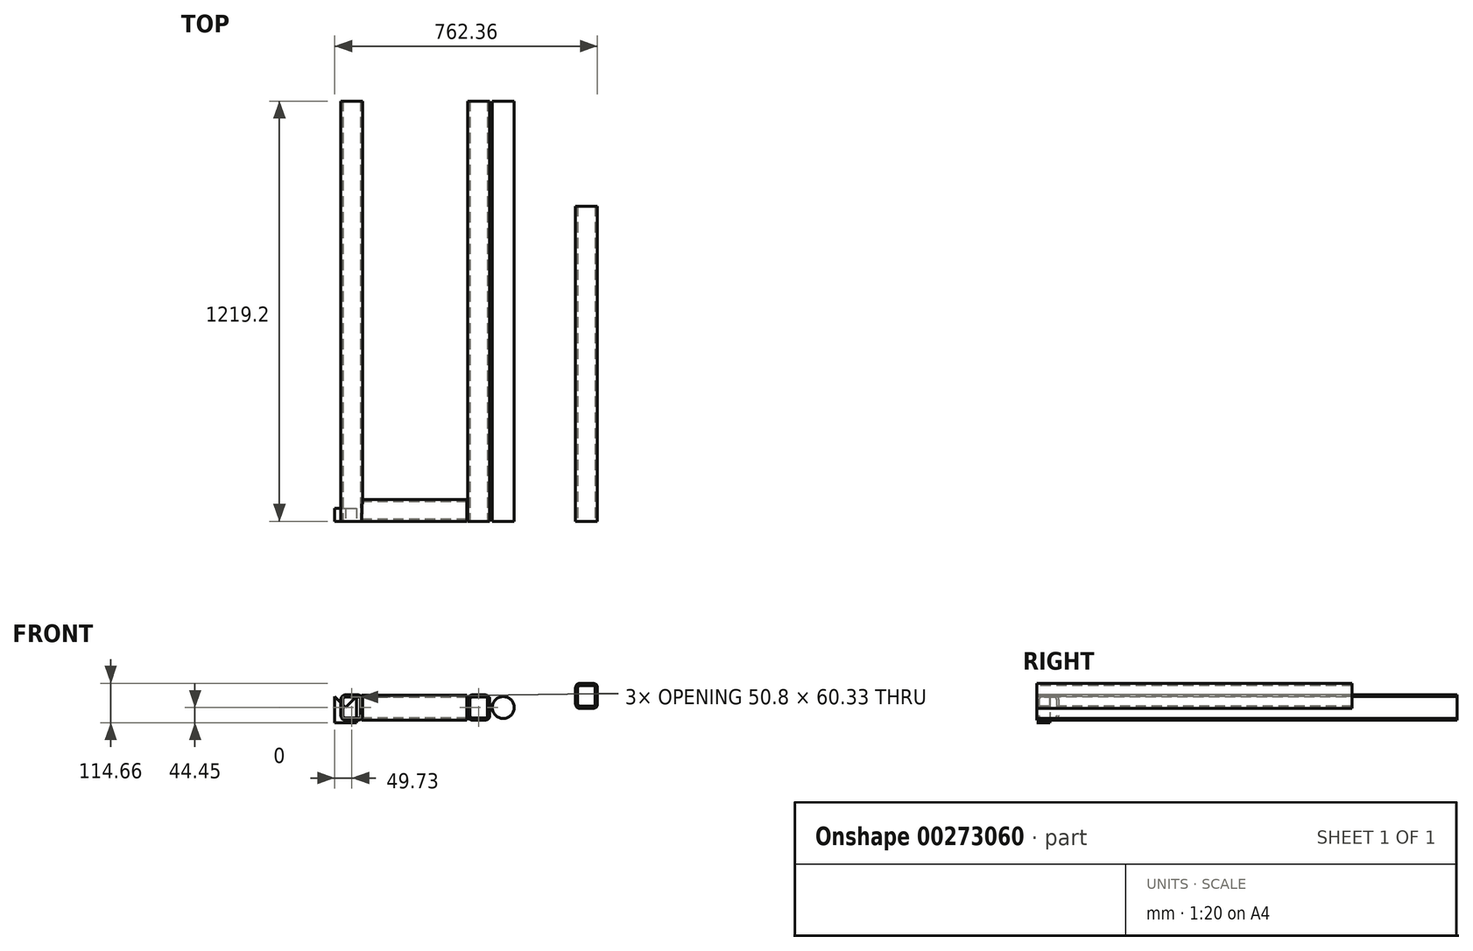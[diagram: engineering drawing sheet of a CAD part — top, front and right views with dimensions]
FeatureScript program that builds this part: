
annotation { "Feature Type Name" : "Feature", "Feature Type Description" : "" }
export const myFeature = defineFeature(function(context is Context, id is Id, definition is map)
    precondition{}
    {
        {
            var Q0;
            Q0=qCreatedBy(makeId("Front.planeOp"),FACE);
            var sketch = newSketch(context, id + "F0", { "sketchPlane" : qUnion([Q0])});
            skLineSegment(sketch, "E0.bottom", {"start": v(-19.05, 36.51) * mm, "end": v(19.05, 36.51) * mm});
            skLineSegment(sketch, "E0.top", {"start": v(-19.05, -36.51) * mm, "end": v(19.05, -36.51) * mm});
            skLineSegment(sketch, "E0.left", {"start": v(-31.75, 23.81) * mm, "end": v(-31.75, -23.81) * mm});
            skLineSegment(sketch, "E0.right", {"start": v(31.75, 23.81) * mm, "end": v(31.75, -23.81) * mm});
            skLineSegment(sketch, "E1.bottom", {"start": v(-19.05, 30.16) * mm, "end": v(19.05, 30.16) * mm});
            skLineSegment(sketch, "E1.top", {"start": v(-19.05, -30.16) * mm, "end": v(19.05, -30.16) * mm});
            skLineSegment(sketch, "E1.left", {"start": v(-25.4, 23.81) * mm, "end": v(-25.4, -23.81) * mm});
            skLineSegment(sketch, "E1.right", {"start": v(25.4, 23.81) * mm, "end": v(25.4, -23.81) * mm});
            skPoint(sketch, "E2.visualSharp", {"position": v(-25.4, 30.16) * mm});
            skArc(sketch, "E2.filletArc", {"start": v(-19.05, 30.16) * mm, "mid": v(-23.54, 28.3) * mm, "end": v(-25.4, 23.81) * mm});
            skPoint(sketch, "E3.visualSharp", {"position": v(-25.4, -30.16) * mm});
            skArc(sketch, "E3.filletArc", {"start": v(-25.4, -23.81) * mm, "mid": v(-23.54, -28.3) * mm, "end": v(-19.05, -30.16) * mm});
            skPoint(sketch, "E4.visualSharp", {"position": v(25.4, -30.16) * mm});
            skArc(sketch, "E4.filletArc", {"start": v(19.05, -30.16) * mm, "mid": v(23.54, -28.3) * mm, "end": v(25.4, -23.81) * mm});
            skPoint(sketch, "E5.visualSharp", {"position": v(25.4, 30.16) * mm});
            skArc(sketch, "E5.filletArc", {"start": v(25.4, 23.81) * mm, "mid": v(23.54, 28.3) * mm, "end": v(19.05, 30.16) * mm});
            skPoint(sketch, "E6.visualSharp", {"position": v(-31.75, 36.51) * mm});
            skArc(sketch, "E6.filletArc", {"start": v(-19.05, 36.51) * mm, "mid": v(-28.03, 32.8) * mm, "end": v(-31.75, 23.81) * mm});
            skPoint(sketch, "E7.visualSharp", {"position": v(-31.75, -36.51) * mm});
            skArc(sketch, "E7.filletArc", {"start": v(-31.75, -23.81) * mm, "mid": v(-28.03, -32.8) * mm, "end": v(-19.05, -36.51) * mm});
            skPoint(sketch, "E8.visualSharp", {"position": v(31.75, -36.51) * mm});
            skArc(sketch, "E8.filletArc", {"start": v(19.05, -36.51) * mm, "mid": v(28.03, -32.8) * mm, "end": v(31.75, -23.81) * mm});
            skPoint(sketch, "E9.visualSharp", {"position": v(31.75, 36.51) * mm});
            skArc(sketch, "E9.filletArc", {"start": v(31.75, 23.81) * mm, "mid": v(28.03, 32.8) * mm, "end": v(19.05, 36.51) * mm});
            skSolve(sketch);
        }
        {
            var Q0;
            Q0=makeQuery(id+"F0.imprint","IMPRINT",FACE,{"disambiguationData":[TD([[makeQuery(id+"F0.imprint","IMPRINT",EDGE,{"derivedFrom":sQuery(id+"F0.wireOp",EDGE,"E0.bottom")}),-1.0]])]});
            extrude(context, id + "F1", {"entities" : qUnion([Q0]), "oppositeDirection" : true, "depth" : 1219.2 * mm});
        }
        {
            var Q0;
            Q0=qCreatedBy(makeId("Front.planeOp"),FACE);
            var sketch = newSketch(context, id + "F2", { "sketchPlane" : qUnion([Q0])});
            skLineSegment(sketch, "E10.bottom", {"start": v(-174.05, 36.05) * mm, "end": v(-135.95, 36.05) * mm});
            skLineSegment(sketch, "E10.top", {"start": v(-174.05, -36.98) * mm, "end": v(-135.95, -36.98) * mm});
            skLineSegment(sketch, "E10.left", {"start": v(-186.75, 23.35) * mm, "end": v(-186.75, -24.28) * mm});
            skLineSegment(sketch, "E10.right", {"start": v(-123.25, 23.35) * mm, "end": v(-123.25, -24.28) * mm});
            skLineSegment(sketch, "E11.bottom", {"start": v(-174.05, 29.7) * mm, "end": v(-135.95, 29.7) * mm});
            skLineSegment(sketch, "E11.top", {"start": v(-174.05, -30.63) * mm, "end": v(-135.95, -30.63) * mm});
            skLineSegment(sketch, "E11.left", {"start": v(-180.4, 23.35) * mm, "end": v(-180.4, -24.28) * mm});
            skLineSegment(sketch, "E11.right", {"start": v(-129.6, 23.35) * mm, "end": v(-129.6, -24.28) * mm});
            skPoint(sketch, "E12.visualSharp", {"position": v(-180.4, 29.7) * mm});
            skArc(sketch, "E12.filletArc", {"start": v(-174.05, 29.7) * mm, "mid": v(-178.54, 27.84) * mm, "end": v(-180.4, 23.35) * mm});
            skPoint(sketch, "E13.visualSharp", {"position": v(-180.4, -30.63) * mm});
            skArc(sketch, "E13.filletArc", {"start": v(-180.4, -24.28) * mm, "mid": v(-178.54, -28.77) * mm, "end": v(-174.05, -30.63) * mm});
            skPoint(sketch, "E14.visualSharp", {"position": v(-129.6, -30.63) * mm});
            skArc(sketch, "E14.filletArc", {"start": v(-135.95, -30.63) * mm, "mid": v(-131.46, -28.77) * mm, "end": v(-129.6, -24.28) * mm});
            skPoint(sketch, "E15.visualSharp", {"position": v(-129.6, 29.7) * mm});
            skArc(sketch, "E15.filletArc", {"start": v(-129.6, 23.35) * mm, "mid": v(-131.46, 27.84) * mm, "end": v(-135.95, 29.7) * mm});
            skPoint(sketch, "E16.visualSharp", {"position": v(-186.75, 36.05) * mm});
            skArc(sketch, "E16.filletArc", {"start": v(-174.05, 36.05) * mm, "mid": v(-183.03, 32.33) * mm, "end": v(-186.75, 23.35) * mm});
            skPoint(sketch, "E17.visualSharp", {"position": v(-186.75, -36.98) * mm});
            skArc(sketch, "E17.filletArc", {"start": v(-186.75, -24.28) * mm, "mid": v(-183.03, -33.26) * mm, "end": v(-174.05, -36.98) * mm});
            skPoint(sketch, "E18.visualSharp", {"position": v(-123.25, -36.98) * mm});
            skArc(sketch, "E18.filletArc", {"start": v(-135.95, -36.98) * mm, "mid": v(-126.97, -33.26) * mm, "end": v(-123.25, -24.28) * mm});
            skPoint(sketch, "E19.visualSharp", {"position": v(-123.25, 36.05) * mm});
            skArc(sketch, "E19.filletArc", {"start": v(-123.25, 23.35) * mm, "mid": v(-126.97, 32.33) * mm, "end": v(-135.95, 36.05) * mm});
            skSolve(sketch);
        }
        {
            var Q0;
            Q0 = qSketchRegion(id + "F2", true);
            extrude(context, id + "F3", {"entities" : qUnion([Q0]), "oppositeDirection" : true, "depth" : 304.8 * mm});
        }
        {
            var Q0;
            Q0=qCreatedBy(makeId("Front.planeOp"),FACE);
            var sketch = newSketch(context, id + "F4", { "sketchPlane" : qUnion([Q0])});
            skLineSegment(sketch, "E20.top", {"start": v(-354.53, -44.45) * mm, "end": v(-291.03, -44.45) * mm});
            skLineSegment(sketch, "E20.left", {"start": v(-354.53, 31.75) * mm, "end": v(-354.53, -44.45) * mm});
            skLineSegment(sketch, "E20.right", {"start": v(-291.03, 31.75) * mm, "end": v(-291.03, -44.45) * mm});
            skLineSegment(sketch, "E21", {"start": v(-354.53, 31.75) * mm, "end": v(-322.78, 0) * mm});
            skPoint(sketch, "E21.endSnap0", {"position": v(-322.78, -44.45) * mm});
            skLineSegment(sketch, "E22", {"start": v(-322.78, 0) * mm, "end": v(-291.03, 31.75) * mm});
            skSolve(sketch);
        }
        {
            var Q0;
            Q0 = qSketchRegion(id + "F4", true);
            extrude(context, id + "F5", {"entities" : qUnion([Q0]), "oppositeDirection" : true, "depth" : 38.1 * mm});
        }
        {
            var Q0;
            Q0=qCreatedBy(makeId("Front.planeOp"),FACE);
            var sketch = newSketch(context, id + "F6", { "sketchPlane" : qUnion([Q0])});
            skCircle(sketch, "E23", {"center": v(134.53, 0) * mm, "radius": 31.75 * mm});
            skSolve(sketch);
        }
        {
            var Q0;
            Q0 = qSketchRegion(id + "F6", true);
            extrude(context, id + "F7", {"entities" : qUnion([Q0]), "oppositeDirection" : true, "depth" : 1219.2 * mm});
        }
        {
            var Q0;
            Q0=qCreatedBy(makeId("Front.planeOp"),FACE);
            var sketch = newSketch(context, id + "F8", { "sketchPlane" : qUnion([Q0])});
            skLineSegment(sketch, "E24.bottom", {"start": v(357.03, 70.21) * mm, "end": v(395.13, 70.21) * mm});
            skLineSegment(sketch, "E24.top", {"start": v(357.03, -2.81) * mm, "end": v(395.13, -2.81) * mm});
            skLineSegment(sketch, "E24.left", {"start": v(344.33, 57.51) * mm, "end": v(344.33, 9.89) * mm});
            skLineSegment(sketch, "E24.right", {"start": v(407.83, 57.51) * mm, "end": v(407.83, 9.89) * mm});
            skLineSegment(sketch, "E25.bottom", {"start": v(357.03, 63.86) * mm, "end": v(395.13, 63.86) * mm});
            skLineSegment(sketch, "E25.top", {"start": v(357.03, 3.54) * mm, "end": v(395.13, 3.54) * mm});
            skLineSegment(sketch, "E25.left", {"start": v(350.68, 57.51) * mm, "end": v(350.68, 9.89) * mm});
            skLineSegment(sketch, "E25.right", {"start": v(401.48, 57.51) * mm, "end": v(401.48, 9.89) * mm});
            skPoint(sketch, "E26.visualSharp", {"position": v(350.68, 63.86) * mm});
            skArc(sketch, "E26.filletArc", {"start": v(357.03, 63.86) * mm, "mid": v(352.54, 62) * mm, "end": v(350.68, 57.51) * mm});
            skPoint(sketch, "E27.visualSharp", {"position": v(350.68, 3.54) * mm});
            skArc(sketch, "E27.filletArc", {"start": v(350.68, 9.89) * mm, "mid": v(352.54, 5.4) * mm, "end": v(357.03, 3.54) * mm});
            skPoint(sketch, "E28.visualSharp", {"position": v(401.48, 3.54) * mm});
            skArc(sketch, "E28.filletArc", {"start": v(395.13, 3.54) * mm, "mid": v(399.62, 5.4) * mm, "end": v(401.48, 9.89) * mm});
            skPoint(sketch, "E29.visualSharp", {"position": v(401.48, 63.86) * mm});
            skArc(sketch, "E29.filletArc", {"start": v(401.48, 57.51) * mm, "mid": v(399.62, 62) * mm, "end": v(395.13, 63.86) * mm});
            skPoint(sketch, "E30.visualSharp", {"position": v(344.33, 70.21) * mm});
            skArc(sketch, "E30.filletArc", {"start": v(357.03, 70.21) * mm, "mid": v(348.05, 66.5) * mm, "end": v(344.33, 57.51) * mm});
            skPoint(sketch, "E31.visualSharp", {"position": v(344.33, -2.81) * mm});
            skArc(sketch, "E31.filletArc", {"start": v(344.33, 9.89) * mm, "mid": v(348.05, 0.9) * mm, "end": v(357.03, -2.81) * mm});
            skPoint(sketch, "E32.visualSharp", {"position": v(407.83, -2.81) * mm});
            skArc(sketch, "E32.filletArc", {"start": v(395.13, -2.81) * mm, "mid": v(404.1, 0.9) * mm, "end": v(407.83, 9.89) * mm});
            skPoint(sketch, "E33.visualSharp", {"position": v(407.83, 70.21) * mm});
            skArc(sketch, "E33.filletArc", {"start": v(407.83, 57.51) * mm, "mid": v(404.1, 66.5) * mm, "end": v(395.13, 70.21) * mm});
            skSolve(sketch);
        }
        {
            var Q0;
            Q0 = qSketchRegion(id + "F8", true);
            extrude(context, id + "F9", {"entities" : qUnion([Q0]), "oppositeDirection" : true, "depth" : 914.4 * mm});
        }
        {
            var Q0;
            Q0=makeQuery(id+"F1.opExtrude","SWEPT_BODY",BODY,{"disambiguationData":[OSD([sQuery(id+"F0.wireOp",EDGE,"E0.bottom"),sQuery(id+"F0.wireOp",EDGE,"E0.top"),sQuery(id+"F0.wireOp",EDGE,"E0.left"),sQuery(id+"F0.wireOp",EDGE,"E0.right"),sQuery(id+"F0.wireOp",EDGE,"E1.bottom"),sQuery(id+"F0.wireOp",EDGE,"E1.top"),sQuery(id+"F0.wireOp",EDGE,"E1.left"),sQuery(id+"F0.wireOp",EDGE,"E1.right"),sQuery(id+"F0.wireOp",EDGE,"E2.filletArc"),sQuery(id+"F0.wireOp",EDGE,"E3.filletArc"),sQuery(id+"F0.wireOp",EDGE,"E4.filletArc"),sQuery(id+"F0.wireOp",EDGE,"E5.filletArc"),sQuery(id+"F0.wireOp",EDGE,"E6.filletArc"),sQuery(id+"F0.wireOp",EDGE,"E7.filletArc"),sQuery(id+"F0.wireOp",EDGE,"E8.filletArc"),sQuery(id+"F0.wireOp",EDGE,"E9.filletArc")])]});
            var Q1;
            Q1=qCreatedBy(id+"FufiWdqUGBMApPi.pointOp",VERTEX);
            var Q2;
            Q2=makeQuery(id+"F5.opExtrude","CAP_EDGE",EDGE,{"disambiguationData":[OSD([sQuery(id+"F4.wireOp",EDGE,"E20.top")])],"isStart":true});
            transform(context, id + "F10", {"entities" : qUnion([Q0]), "transformType" : TransformType.TRANSLATION_ENTITY, "oppositeDirectionEntity" : false, "transformLine" : qUnion([Q1, Q2]), "makeCopy" : true});
        }
        {
            var Q0;
            Q0=makeQuery(id+"F1.opExtrude","SWEPT_BODY",BODY,{"disambiguationData":[OSD([sQuery(id+"F0.wireOp",EDGE,"E0.bottom"),sQuery(id+"F0.wireOp",EDGE,"E0.top"),sQuery(id+"F0.wireOp",EDGE,"E0.left"),sQuery(id+"F0.wireOp",EDGE,"E0.right"),sQuery(id+"F0.wireOp",EDGE,"E1.bottom"),sQuery(id+"F0.wireOp",EDGE,"E1.top"),sQuery(id+"F0.wireOp",EDGE,"E1.left"),sQuery(id+"F0.wireOp",EDGE,"E1.right"),sQuery(id+"F0.wireOp",EDGE,"E2.filletArc"),sQuery(id+"F0.wireOp",EDGE,"E3.filletArc"),sQuery(id+"F0.wireOp",EDGE,"E4.filletArc"),sQuery(id+"F0.wireOp",EDGE,"E5.filletArc"),sQuery(id+"F0.wireOp",EDGE,"E6.filletArc"),sQuery(id+"F0.wireOp",EDGE,"E7.filletArc"),sQuery(id+"F0.wireOp",EDGE,"E8.filletArc"),sQuery(id+"F0.wireOp",EDGE,"E9.filletArc")])]});
            var Q1;
            Q1=makeQuery(id+"F1.opExtrude","CAP_EDGE",EDGE,{"disambiguationData":[OSD([sQuery(id+"F0.wireOp",EDGE,"E0.bottom")])],"isStart":true});
            transform(context, id + "F11", {"entities" : qUnion([Q0]), "transformType" : TransformType.TRANSLATION_DISTANCE, "transformDirection" : qUnion([Q1]), "distance" : 304.8 * mm, "oppositeDirection" : true, "makeCopy" : false});
        }
        {
            var Q0;
            Q0=makeQuery(id+"F3.opExtrude","SWEPT_BODY",BODY,{"disambiguationData":[OSD([sQuery(id+"F2.wireOp",EDGE,"E10.bottom"),sQuery(id+"F2.wireOp",EDGE,"E10.top"),sQuery(id+"F2.wireOp",EDGE,"E10.left"),sQuery(id+"F2.wireOp",EDGE,"E10.right"),sQuery(id+"F2.wireOp",EDGE,"E11.bottom"),sQuery(id+"F2.wireOp",EDGE,"E11.top"),sQuery(id+"F2.wireOp",EDGE,"E11.left"),sQuery(id+"F2.wireOp",EDGE,"E11.right"),sQuery(id+"F2.wireOp",EDGE,"E12.filletArc"),sQuery(id+"F2.wireOp",EDGE,"E13.filletArc"),sQuery(id+"F2.wireOp",EDGE,"E14.filletArc"),sQuery(id+"F2.wireOp",EDGE,"E15.filletArc"),sQuery(id+"F2.wireOp",EDGE,"E16.filletArc"),sQuery(id+"F2.wireOp",EDGE,"E17.filletArc"),sQuery(id+"F2.wireOp",EDGE,"E18.filletArc"),sQuery(id+"F2.wireOp",EDGE,"E19.filletArc")])]});
            var Q1;
            Q1=makeQuery(id+"F3.opExtrude","CAP_EDGE",EDGE,{"disambiguationData":[OSD([sQuery(id+"F2.wireOp",EDGE,"E10.left")])],"isStart":true});
            transform(context, id + "F12", {"entities" : qUnion([Q0]), "transformType" : TransformType.ROTATION, "transformAxis" : qUnion([Q1]), "angle" : 90 * degree, "makeCopy" : false});
        }
        {
            var Q0;
            Q0=makeQuery(id+"F3.opExtrude","SWEPT_BODY",BODY,{"disambiguationData":[OSD([sQuery(id+"F2.wireOp",EDGE,"E10.bottom"),sQuery(id+"F2.wireOp",EDGE,"E10.top"),sQuery(id+"F2.wireOp",EDGE,"E10.left"),sQuery(id+"F2.wireOp",EDGE,"E10.right"),sQuery(id+"F2.wireOp",EDGE,"E11.bottom"),sQuery(id+"F2.wireOp",EDGE,"E11.top"),sQuery(id+"F2.wireOp",EDGE,"E11.left"),sQuery(id+"F2.wireOp",EDGE,"E11.right"),sQuery(id+"F2.wireOp",EDGE,"E12.filletArc"),sQuery(id+"F2.wireOp",EDGE,"E13.filletArc"),sQuery(id+"F2.wireOp",EDGE,"E14.filletArc"),sQuery(id+"F2.wireOp",EDGE,"E15.filletArc"),sQuery(id+"F2.wireOp",EDGE,"E16.filletArc"),sQuery(id+"F2.wireOp",EDGE,"E17.filletArc"),sQuery(id+"F2.wireOp",EDGE,"E18.filletArc"),sQuery(id+"F2.wireOp",EDGE,"E19.filletArc")])]});
            var Q1;
            Q1=makeQuery(id+"F3.opExtrude","SWEPT_EDGE",EDGE,{"disambiguationData":[OSD([sQuery(id+"F2.wireOp",EDGE,"E10.right"),sQuery(id+"F2.wireOp",EDGE,"E19.filletArc")])]});
            transform(context, id + "F13", {"entities" : qUnion([Q0]), "transformType" : TransformType.TRANSLATION_DISTANCE, "transformDirection" : qUnion([Q1]), "distance" : 88.9 * mm, "makeCopy" : false});
        }
        {
            var Q0;
            Q0=makeQuery(id+"F3.opExtrude","SWEPT_BODY",BODY,{"disambiguationData":[OSD([sQuery(id+"F2.wireOp",EDGE,"E10.bottom"),sQuery(id+"F2.wireOp",EDGE,"E10.top"),sQuery(id+"F2.wireOp",EDGE,"E10.left"),sQuery(id+"F2.wireOp",EDGE,"E10.right"),sQuery(id+"F2.wireOp",EDGE,"E11.bottom"),sQuery(id+"F2.wireOp",EDGE,"E11.top"),sQuery(id+"F2.wireOp",EDGE,"E11.left"),sQuery(id+"F2.wireOp",EDGE,"E11.right"),sQuery(id+"F2.wireOp",EDGE,"E12.filletArc"),sQuery(id+"F2.wireOp",EDGE,"E13.filletArc"),sQuery(id+"F2.wireOp",EDGE,"E14.filletArc"),sQuery(id+"F2.wireOp",EDGE,"E15.filletArc"),sQuery(id+"F2.wireOp",EDGE,"E16.filletArc"),sQuery(id+"F2.wireOp",EDGE,"E17.filletArc"),sQuery(id+"F2.wireOp",EDGE,"E18.filletArc"),sQuery(id+"F2.wireOp",EDGE,"E19.filletArc")])]});
            var Q1;
            Q1=makeQuery(id+"F3.opExtrude","CAP_EDGE",EDGE,{"disambiguationData":[OSD([sQuery(id+"F2.wireOp",EDGE,"E10.bottom")])],"isStart":false});
            transform(context, id + "F14", {"entities" : qUnion([Q0]), "transformType" : TransformType.TRANSLATION_DISTANCE, "transformDirection" : qUnion([Q1]), "distance" : 63.5 * mm, "oppositeDirection" : true, "makeCopy" : false});
        }
        {
            var Q0;
            Q0=makeQuery(id+"F1.opExtrude","SWEPT_BODY",BODY,{"disambiguationData":[OSD([sQuery(id+"F0.wireOp",EDGE,"E0.bottom"),sQuery(id+"F0.wireOp",EDGE,"E0.top"),sQuery(id+"F0.wireOp",EDGE,"E0.left"),sQuery(id+"F0.wireOp",EDGE,"E0.right"),sQuery(id+"F0.wireOp",EDGE,"E1.bottom"),sQuery(id+"F0.wireOp",EDGE,"E1.top"),sQuery(id+"F0.wireOp",EDGE,"E1.left"),sQuery(id+"F0.wireOp",EDGE,"E1.right"),sQuery(id+"F0.wireOp",EDGE,"E2.filletArc"),sQuery(id+"F0.wireOp",EDGE,"E3.filletArc"),sQuery(id+"F0.wireOp",EDGE,"E4.filletArc"),sQuery(id+"F0.wireOp",EDGE,"E5.filletArc"),sQuery(id+"F0.wireOp",EDGE,"E6.filletArc"),sQuery(id+"F0.wireOp",EDGE,"E7.filletArc"),sQuery(id+"F0.wireOp",EDGE,"E8.filletArc"),sQuery(id+"F0.wireOp",EDGE,"E9.filletArc")])]});
            transform(context, id + "F15", {"entities" : qUnion([Q0]), "transformType" : TransformType.TRANSLATION_3D, "dx" : 0 * mm, "dy" : 0 * mm, "dz" : 0 * mm, "makeCopy" : true});
        }
    });
